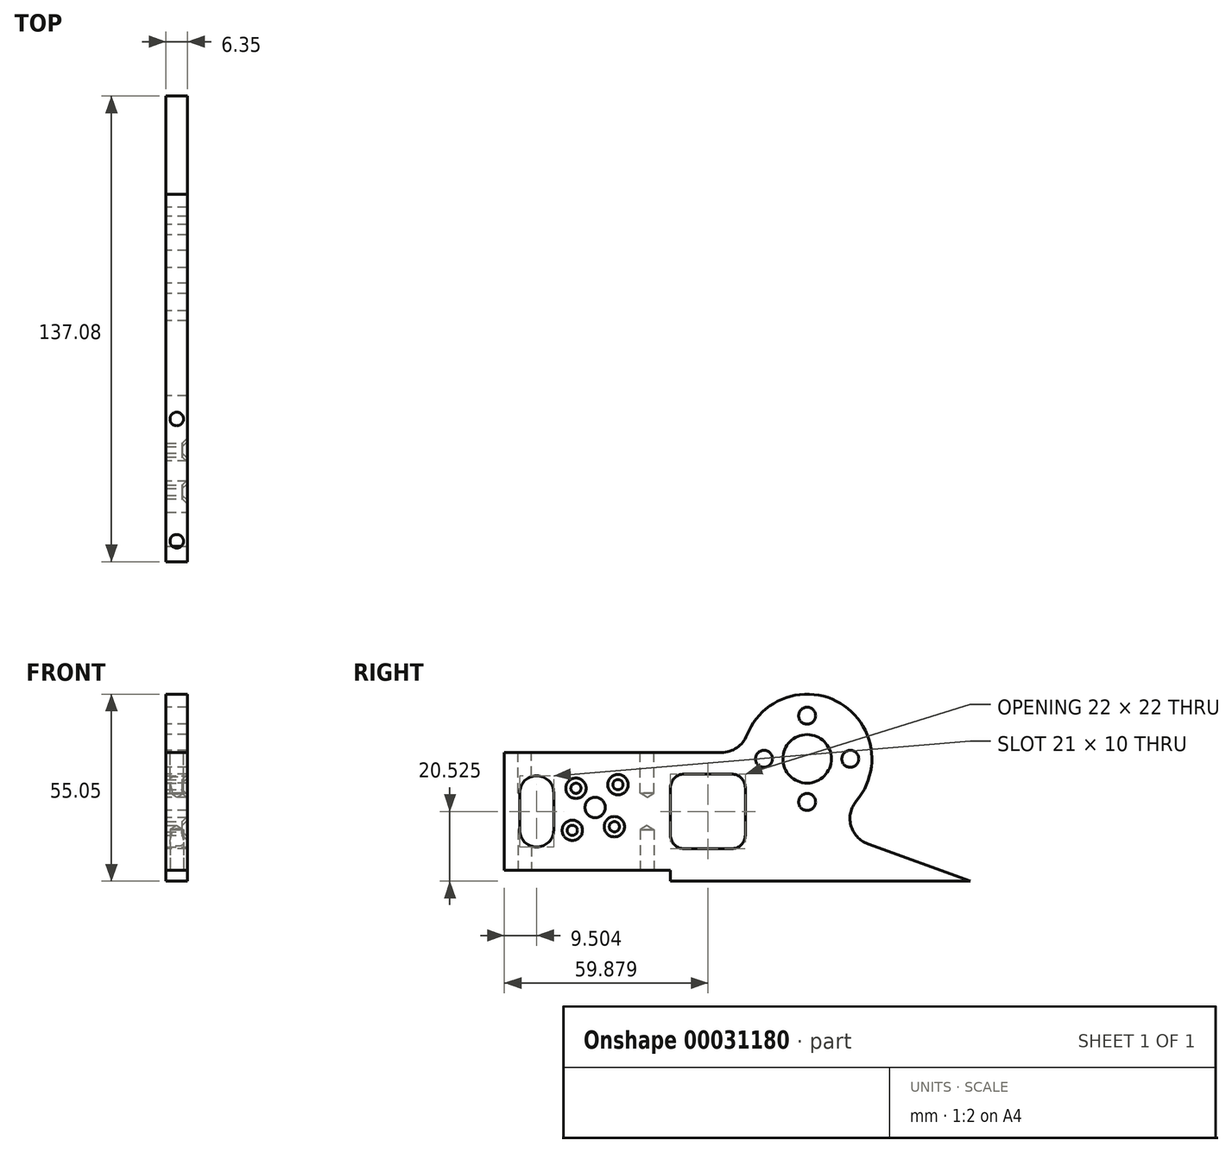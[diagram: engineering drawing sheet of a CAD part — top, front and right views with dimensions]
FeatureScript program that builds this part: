
annotation { "Feature Type Name" : "Feature", "Feature Type Description" : "" }
export const myFeature = defineFeature(function(context is Context, id is Id, definition is map)
    precondition{}
    {
        {
            var Q0;
            Q0=qCreatedBy(makeId("Right.planeOp"),FACE);
            var sketch = newSketch(context, id + "F0", { "sketchPlane" : qUnion([Q0])});
            skCircle(sketch, "E0", {"center": v(0, 0) * mm, "radius": 7.14 * mm});
            skArc(sketch, "E1", {"start": v(14.52, -12.34) * mm, "mid": v(9.78, 16.35) * mm, "end": v(-17.74, 6.95) * mm});
            skCircle(sketch, "E2", {"center": v(0, 0) * mm, "radius": 12.7 * mm, "construction": true});
            skCircle(sketch, "E3", {"center": v(0, 12.7) * mm, "radius": 2.5 * mm});
            skCircle(sketch, "E4", {"center": v(-12.7, 0) * mm, "radius": 2.5 * mm});
            skCircle(sketch, "E5", {"center": v(12.7, 0) * mm, "radius": 2.5 * mm});
            skCircle(sketch, "E6", {"center": v(0, -12.7) * mm, "radius": 2.5 * mm});
            skCircle(sketch, "E7", {"center": v(0, 0) * mm, "radius": 33.85 * mm, "construction": true});
            skLineSegment(sketch, "E8", {"start": v(48, -36) * mm, "end": v(17.88, -25.04) * mm});
            skArc(sketch, "E9.filletArc", {"start": v(14.52, -12.34) * mm, "mid": v(12.88, -19.56) * mm, "end": v(17.88, -25.04) * mm});
            skLineSegment(sketch, "E10.bottom", {"start": v(-127.08, -4.48) * mm, "end": v(-93.08, -4.48) * mm});
            skLineSegment(sketch, "E10.top", {"start": v(-127.08, -26.48) * mm, "end": v(-93.08, -26.48) * mm});
            skLineSegment(sketch, "E10.right", {"start": v(-89.08, -8.48) * mm, "end": v(-89.08, -22.48) * mm});
            skLineSegment(sketch, "E11", {"start": v(-127.08, 1.87) * mm, "end": v(-127.08, -4.48) * mm});
            skLineSegment(sketch, "E12", {"start": v(-127.08, -26.48) * mm, "end": v(-127.08, -32.83) * mm});
            skLineSegment(sketch, "E13", {"start": v(-127.08, 1.87) * mm, "end": v(-25.18, 1.87) * mm});
            skCircle(sketch, "E14", {"center": v(-62.38, -14.33) * mm, "radius": 14 * mm, "construction": true});
            skLineSegment(sketch, "E15", {"start": v(-62.38, -14.33) * mm, "end": v(-62.38, 1.87) * mm, "construction": true});
            skLineSegment(sketch, "E16", {"start": v(-62.38, -14.33) * mm, "end": v(-62.38, -32.83) * mm, "construction": true});
            skLineSegment(sketch, "E17", {"start": v(-62.38, -14.33) * mm, "end": v(0, 0) * mm, "construction": true});
            skLineSegment(sketch, "E18.bottom", {"start": v(-40.2, 1.87) * mm, "end": v(-46.55, 1.87) * mm, "construction": true});
            skLineSegment(sketch, "E18.top", {"start": v(-40.2, -32.83) * mm, "end": v(-46.55, -32.83) * mm, "construction": true});
            skLineSegment(sketch, "E18.left", {"start": v(-40.2, 1.87) * mm, "end": v(-40.2, -32.83) * mm, "construction": true});
            skLineSegment(sketch, "E18.right", {"start": v(-46.55, 1.87) * mm, "end": v(-46.55, -32.83) * mm, "construction": true});
            skPoint(sketch, "E19.visualSharp", {"position": v(-18.96, 1.87) * mm});
            skArc(sketch, "E19.filletArc", {"start": v(-25.18, 1.87) * mm, "mid": v(-20.68, 3.27) * mm, "end": v(-17.74, 6.95) * mm});
            skPoint(sketch, "E20.visualSharp", {"position": v(-89.08, -4.48) * mm});
            skArc(sketch, "E20.filletArc", {"start": v(-89.08, -8.48) * mm, "mid": v(-90.25, -5.65) * mm, "end": v(-93.08, -4.48) * mm});
            skPoint(sketch, "E21.visualSharp", {"position": v(-89.08, -26.48) * mm});
            skArc(sketch, "E21.filletArc", {"start": v(-93.08, -26.48) * mm, "mid": v(-90.25, -25.3) * mm, "end": v(-89.08, -22.48) * mm});
            skLineSegment(sketch, "E22", {"start": v(-36.2, -4.48) * mm, "end": v(-22.2, -4.48) * mm});
            skLineSegment(sketch, "E23", {"start": v(-18.2, -8.48) * mm, "end": v(-18.2, -22.48) * mm});
            skLineSegment(sketch, "E24", {"start": v(-22.2, -26.48) * mm, "end": v(-36.2, -26.48) * mm});
            skLineSegment(sketch, "E25", {"start": v(-40.2, -22.48) * mm, "end": v(-40.2, -8.48) * mm});
            skPoint(sketch, "E26.visualSharp", {"position": v(-40.2, -4.48) * mm});
            skArc(sketch, "E26.filletArc", {"start": v(-36.2, -4.48) * mm, "mid": v(-39.03, -5.65) * mm, "end": v(-40.2, -8.48) * mm});
            skPoint(sketch, "E27.visualSharp", {"position": v(-18.2, -4.48) * mm});
            skArc(sketch, "E27.filletArc", {"start": v(-18.2, -8.48) * mm, "mid": v(-19.37, -5.65) * mm, "end": v(-22.2, -4.48) * mm});
            skPoint(sketch, "E28.visualSharp", {"position": v(-18.2, -26.48) * mm});
            skArc(sketch, "E28.filletArc", {"start": v(-22.2, -26.47) * mm, "mid": v(-19.37, -25.3) * mm, "end": v(-18.2, -22.48) * mm});
            skPoint(sketch, "E29.visualSharp", {"position": v(-40.2, -26.48) * mm});
            skArc(sketch, "E29.filletArc", {"start": v(-40.2, -22.48) * mm, "mid": v(-39.03, -25.3) * mm, "end": v(-36.2, -26.48) * mm});
            skCircle(sketch, "E30", {"center": v(-62.38, -14.33) * mm, "radius": 3 * mm});
            skLineSegment(sketch, "E31", {"start": v(-40.2, -32.83) * mm, "end": v(-127.08, -32.83) * mm});
            skLineSegment(sketch, "E32", {"start": v(-40.2, -32.83) * mm, "end": v(-40.2, -36) * mm});
            skLineSegment(sketch, "E33", {"start": v(-40.2, -36) * mm, "end": v(48, -36) * mm});
            skSolve(sketch);
        }
        {
            var Q0;
            Q0 = qSketchRegion(id + "F0", true);
            extrude(context, id + "F1", {"entities" : qUnion([Q0]), "depth" : 6.35 * mm});
        }
        {
            var Q0;
            Q0=makeQuery(id+"F1.opExtrude","CAP_FACE",FACE,{"disambiguationData":[OSD([sQuery(id+"F0.wireOp",EDGE,"E0"),sQuery(id+"F0.wireOp",EDGE,"E1"),sQuery(id+"F0.wireOp",EDGE,"E3"),sQuery(id+"F0.wireOp",EDGE,"E4"),sQuery(id+"F0.wireOp",EDGE,"E5"),sQuery(id+"F0.wireOp",EDGE,"E6"),sQuery(id+"F0.wireOp",EDGE,"d800da94-32d5-4916-a3c5-9d9b6c6d528f"),sQuery(id+"F0.wireOp",EDGE,"E8"),sQuery(id+"F0.wireOp",EDGE,"E9.filletArc"),sQuery(id+"F0.wireOp",EDGE,"E10.bottom"),sQuery(id+"F0.wireOp",EDGE,"E10.top"),sQuery(id+"F0.wireOp",EDGE,"E10.right"),sQuery(id+"F0.wireOp",EDGE,"E11"),sQuery(id+"F0.wireOp",EDGE,"E12"),sQuery(id+"F0.wireOp",EDGE,"E13"),sQuery(id+"F0.wireOp",EDGE,"E19.filletArc"),sQuery(id+"F0.wireOp",EDGE,"E20.filletArc"),sQuery(id+"F0.wireOp",EDGE,"E21.filletArc"),sQuery(id+"F0.wireOp",EDGE,"E22"),sQuery(id+"F0.wireOp",EDGE,"E23"),sQuery(id+"F0.wireOp",EDGE,"E24"),sQuery(id+"F0.wireOp",EDGE,"E25"),sQuery(id+"F0.wireOp",EDGE,"E26.filletArc"),sQuery(id+"F0.wireOp",EDGE,"E27.filletArc"),sQuery(id+"F0.wireOp",EDGE,"E28.filletArc"),sQuery(id+"F0.wireOp",EDGE,"E29.filletArc"),sQuery(id+"F0.wireOp",EDGE,"E30")])],"isStart":false});
            var sketch = newSketch(context, id + "F2", { "sketchPlane" : qUnion([Q0])});
            skCircle(sketch, "E34", {"center": v(-62.38, -14.33) * mm, "radius": 8 * mm, "construction": true});
            skCircle(sketch, "E35", {"center": v(-62.38, -14.33) * mm, "radius": 9.5 * mm, "construction": true});
            skPoint(sketch, "E36", {"position": v(-55.66, -7.6) * mm});
            skPoint(sketch, "E37", {"position": v(-68.03, -8.67) * mm});
            skPoint(sketch, "E38", {"position": v(-69.1, -21.04) * mm});
            skPoint(sketch, "E39", {"position": v(-56.72, -19.98) * mm});
            skLineSegment(sketch, "E40", {"start": v(-68.03, -8.67) * mm, "end": v(-56.72, -19.98) * mm, "construction": true});
            skLineSegment(sketch, "E41", {"start": v(-55.66, -7.6) * mm, "end": v(-69.1, -21.04) * mm, "construction": true});
            skLineSegment(sketch, "E42", {"start": v(-62.38, -14.33) * mm, "end": v(-62.38, 1.87) * mm, "construction": true});
            skSolve(sketch);
        }
        {
            var Q0;
            Q0=sQuery(id+"F2.wireOp",VERTEX,"E36");
            var Q1;
            Q1=sQuery(id+"F2.wireOp",VERTEX,"E37");
            var Q2;
            Q2=sQuery(id+"F2.wireOp",VERTEX,"E38");
            var Q3;
            Q3=sQuery(id+"F2.wireOp",VERTEX,"E39");
            var Q4;
            Q4=makeQuery(id+"F1.opExtrude","SWEPT_BODY",BODY,{"disambiguationData":[OSD([sQuery(id+"F0.wireOp",EDGE,"E0"),sQuery(id+"F0.wireOp",EDGE,"E1"),sQuery(id+"F0.wireOp",EDGE,"E3"),sQuery(id+"F0.wireOp",EDGE,"E4"),sQuery(id+"F0.wireOp",EDGE,"E5"),sQuery(id+"F0.wireOp",EDGE,"E6"),sQuery(id+"F0.wireOp",EDGE,"d800da94-32d5-4916-a3c5-9d9b6c6d528f"),sQuery(id+"F0.wireOp",EDGE,"E8"),sQuery(id+"F0.wireOp",EDGE,"E9.filletArc"),sQuery(id+"F0.wireOp",EDGE,"E10.bottom"),sQuery(id+"F0.wireOp",EDGE,"E10.top"),sQuery(id+"F0.wireOp",EDGE,"E10.right"),sQuery(id+"F0.wireOp",EDGE,"E11"),sQuery(id+"F0.wireOp",EDGE,"E12"),sQuery(id+"F0.wireOp",EDGE,"E13"),sQuery(id+"F0.wireOp",EDGE,"E19.filletArc"),sQuery(id+"F0.wireOp",EDGE,"E20.filletArc"),sQuery(id+"F0.wireOp",EDGE,"E21.filletArc"),sQuery(id+"F0.wireOp",EDGE,"E22"),sQuery(id+"F0.wireOp",EDGE,"E23"),sQuery(id+"F0.wireOp",EDGE,"E24"),sQuery(id+"F0.wireOp",EDGE,"E25"),sQuery(id+"F0.wireOp",EDGE,"E26.filletArc"),sQuery(id+"F0.wireOp",EDGE,"E27.filletArc"),sQuery(id+"F0.wireOp",EDGE,"E28.filletArc"),sQuery(id+"F0.wireOp",EDGE,"E29.filletArc"),sQuery(id+"F0.wireOp",EDGE,"E30")])]});
            hole(context, id + "F3", {"style" : HoleStyle.C_SINK, "holeDiameter" : 3 * mm, "cSinkDiameter" : 6 * mm, "endStyle" : HoleEndStyle.THROUGH, "locations" : qUnion([Q0, Q1, Q2, Q3]), "scope" : qUnion([Q4]), "cSinkAngle" : 90 * degree});
        }
        {
            var Q0;
            Q0=makeQuery(id+"F1.opExtrude","CAP_FACE",FACE,{"disambiguationData":[OSD([sQuery(id+"F0.wireOp",EDGE,"E0"),sQuery(id+"F0.wireOp",EDGE,"E1"),sQuery(id+"F0.wireOp",EDGE,"E3"),sQuery(id+"F0.wireOp",EDGE,"E4"),sQuery(id+"F0.wireOp",EDGE,"E5"),sQuery(id+"F0.wireOp",EDGE,"E6"),sQuery(id+"F0.wireOp",EDGE,"d800da94-32d5-4916-a3c5-9d9b6c6d528f"),sQuery(id+"F0.wireOp",EDGE,"E8"),sQuery(id+"F0.wireOp",EDGE,"E9.filletArc"),sQuery(id+"F0.wireOp",EDGE,"E10.bottom"),sQuery(id+"F0.wireOp",EDGE,"E10.top"),sQuery(id+"F0.wireOp",EDGE,"E10.right"),sQuery(id+"F0.wireOp",EDGE,"E11"),sQuery(id+"F0.wireOp",EDGE,"E12"),sQuery(id+"F0.wireOp",EDGE,"E13"),sQuery(id+"F0.wireOp",EDGE,"E19.filletArc"),sQuery(id+"F0.wireOp",EDGE,"E20.filletArc"),sQuery(id+"F0.wireOp",EDGE,"E21.filletArc"),sQuery(id+"F0.wireOp",EDGE,"E22"),sQuery(id+"F0.wireOp",EDGE,"E23"),sQuery(id+"F0.wireOp",EDGE,"E24"),sQuery(id+"F0.wireOp",EDGE,"E25"),sQuery(id+"F0.wireOp",EDGE,"E26.filletArc"),sQuery(id+"F0.wireOp",EDGE,"E27.filletArc"),sQuery(id+"F0.wireOp",EDGE,"E28.filletArc"),sQuery(id+"F0.wireOp",EDGE,"E29.filletArc"),sQuery(id+"F0.wireOp",EDGE,"E30")])],"isStart":false});
            var sketch = newSketch(context, id + "F4", { "sketchPlane" : qUnion([Q0])});
            skLineSegment(sketch, "E43", {"start": v(-79.58, -9.98) * mm, "end": v(-79.58, -20.98) * mm});
            skArc(sketch, "E44.0.startCap", {"start": v(-84.58, -9.98) * mm, "mid": v(-79.58, -4.98) * mm, "end": v(-74.58, -9.98) * mm});
            skArc(sketch, "E44.0.endCap", {"start": v(-74.58, -20.98) * mm, "mid": v(-79.58, -25.98) * mm, "end": v(-84.58, -20.98) * mm});
            skLineSegment(sketch, "E44.0.left", {"start": v(-74.58, -9.98) * mm, "end": v(-74.58, -20.98) * mm});
            skLineSegment(sketch, "E44.0.right", {"start": v(-84.58, -9.98) * mm, "end": v(-84.58, -20.98) * mm});
            skLineSegment(sketch, "E45", {"start": v(-79.58, -9.98) * mm, "end": v(-79.58, 1.87) * mm, "construction": true});
            skLineSegment(sketch, "E46", {"start": v(-79.58, -20.98) * mm, "end": v(-79.58, -32.83) * mm, "construction": true});
            skPoint(sketch, "E46.endSnap0", {"position": v(-79.58, -25.98) * mm});
            skSolve(sketch);
        }
        {
            var Q0;
            Q0 = qSketchRegion(id + "F4", true);
            extrude(context, id + "F5", {"entities" : qUnion([Q0]), "operationType" : NewBodyOperationType.REMOVE, "oppositeDirection" : true, "depth" : 25 * mm});
        }
        {
            var Q0;
            Q0=makeQuery(id+"F1.opExtrude","SWEPT_FACE",FACE,{"disambiguationData":[OSD([sQuery(id+"F0.wireOp",EDGE,"E13")])]});
            var sketch = newSketch(context, id + "F6", { "sketchPlane" : qUnion([Q0])});
            skLineSegment(sketch, "E47.bottom", {"start": v(0, -127.08) * mm, "end": v(6.35, -127.08) * mm});
            skLineSegment(sketch, "E47.top", {"start": v(0, -89.08) * mm, "end": v(6.35, -89.08) * mm});
            skLineSegment(sketch, "E47.left", {"start": v(0, -127.08) * mm, "end": v(0, -89.08) * mm});
            skLineSegment(sketch, "E47.right", {"start": v(6.35, -127.08) * mm, "end": v(6.35, -89.08) * mm});
            skSolve(sketch);
        }
        {
            var Q0;
            Q0 = qSketchRegion(id + "F6", true);
            extrude(context, id + "F7", {"entities" : qUnion([Q0]), "operationType" : NewBodyOperationType.REMOVE, "endBound" : BoundingType.THROUGH_ALL, "oppositeDirection" : true, "depth" : 25 * mm});
        }
        {
            var Q0;
            Q0=makeQuery(id+"F1.opExtrude","SWEPT_FACE",FACE,{"disambiguationData":[OSD([sQuery(id+"F0.wireOp",EDGE,"E13")])]});
            var sketch = newSketch(context, id + "F8", { "sketchPlane" : qUnion([Q0])});
            skPoint(sketch, "E48", {"position": v(3.18, -83.08) * mm});
            skPoint(sketch, "E49", {"position": v(3.17, -47.08) * mm});
            skLineSegment(sketch, "E50", {"start": v(3.18, -89.08) * mm, "end": v(3.18, -83.08) * mm, "construction": true});
            skLineSegment(sketch, "E51", {"start": v(3.17, -47.08) * mm, "end": v(3.18, -83.08) * mm, "construction": true});
            skSolve(sketch);
        }
        {
            var Q0;
            Q0=sQuery(id+"F8.wireOp",VERTEX,"E49");
            var Q1;
            Q1=sQuery(id+"F8.wireOp",VERTEX,"E48");
            var Q2;
            Q2=makeQuery(id+"F1.opExtrude","SWEPT_BODY",BODY,{"disambiguationData":[OSD([sQuery(id+"F0.wireOp",EDGE,"E0"),sQuery(id+"F0.wireOp",EDGE,"E1"),sQuery(id+"F0.wireOp",EDGE,"E3"),sQuery(id+"F0.wireOp",EDGE,"E4"),sQuery(id+"F0.wireOp",EDGE,"E5"),sQuery(id+"F0.wireOp",EDGE,"E6"),sQuery(id+"F0.wireOp",EDGE,"E8"),sQuery(id+"F0.wireOp",EDGE,"E9.filletArc"),sQuery(id+"F0.wireOp",EDGE,"E10.bottom"),sQuery(id+"F0.wireOp",EDGE,"E10.top"),sQuery(id+"F0.wireOp",EDGE,"E10.right"),sQuery(id+"F0.wireOp",EDGE,"E11"),sQuery(id+"F0.wireOp",EDGE,"E12"),sQuery(id+"F0.wireOp",EDGE,"E13"),sQuery(id+"F0.wireOp",EDGE,"E19.filletArc"),sQuery(id+"F0.wireOp",EDGE,"E20.filletArc"),sQuery(id+"F0.wireOp",EDGE,"E21.filletArc"),sQuery(id+"F0.wireOp",EDGE,"E22"),sQuery(id+"F0.wireOp",EDGE,"E23"),sQuery(id+"F0.wireOp",EDGE,"E24"),sQuery(id+"F0.wireOp",EDGE,"E25"),sQuery(id+"F0.wireOp",EDGE,"E26.filletArc"),sQuery(id+"F0.wireOp",EDGE,"E27.filletArc"),sQuery(id+"F0.wireOp",EDGE,"E28.filletArc"),sQuery(id+"F0.wireOp",EDGE,"E29.filletArc"),sQuery(id+"F0.wireOp",EDGE,"E30"),sQuery(id+"F0.wireOp",EDGE,"E31"),sQuery(id+"F0.wireOp",EDGE,"E32"),sQuery(id+"F0.wireOp",EDGE,"E33")])]});
            hole(context, id + "F9", {"style" : HoleStyle.SIMPLE, "holeDiameter" : 4 * mm, "endStyle" : HoleEndStyle.BLIND, "holeDepth" : 12 * mm, "locations" : qUnion([Q0, Q1]), "scope" : qUnion([Q2])});
        }
        {
            var Q0;
            Q0=makeQuery(id+"F1.opExtrude","SWEPT_FACE",FACE,{"disambiguationData":[OSD([sQuery(id+"F0.wireOp",EDGE,"E31")])]});
            var sketch = newSketch(context, id + "F10", { "sketchPlane" : qUnion([Q0])});
            skPoint(sketch, "E52", {"position": v(3.18, 47.08) * mm});
            skPoint(sketch, "E53", {"position": v(3.18, 83.08) * mm});
            skLineSegment(sketch, "E54", {"start": v(3.17, 89.08) * mm, "end": v(3.18, 83.08) * mm, "construction": true});
            skLineSegment(sketch, "E55", {"start": v(3.18, 47.08) * mm, "end": v(3.18, 83.08) * mm, "construction": true});
            skSolve(sketch);
        }
        {
            var Q0;
            Q0=sQuery(id+"F10.wireOp",VERTEX,"E52");
            var Q1;
            Q1=sQuery(id+"F10.wireOp",VERTEX,"E53");
            var Q2;
            Q2=makeQuery(id+"F1.opExtrude","SWEPT_BODY",BODY,{"disambiguationData":[OSD([sQuery(id+"F0.wireOp",EDGE,"E0"),sQuery(id+"F0.wireOp",EDGE,"E1"),sQuery(id+"F0.wireOp",EDGE,"E3"),sQuery(id+"F0.wireOp",EDGE,"E4"),sQuery(id+"F0.wireOp",EDGE,"E5"),sQuery(id+"F0.wireOp",EDGE,"E6"),sQuery(id+"F0.wireOp",EDGE,"E8"),sQuery(id+"F0.wireOp",EDGE,"E9.filletArc"),sQuery(id+"F0.wireOp",EDGE,"E10.bottom"),sQuery(id+"F0.wireOp",EDGE,"E10.top"),sQuery(id+"F0.wireOp",EDGE,"E10.right"),sQuery(id+"F0.wireOp",EDGE,"E11"),sQuery(id+"F0.wireOp",EDGE,"E12"),sQuery(id+"F0.wireOp",EDGE,"E13"),sQuery(id+"F0.wireOp",EDGE,"E19.filletArc"),sQuery(id+"F0.wireOp",EDGE,"E20.filletArc"),sQuery(id+"F0.wireOp",EDGE,"E21.filletArc"),sQuery(id+"F0.wireOp",EDGE,"E22"),sQuery(id+"F0.wireOp",EDGE,"E23"),sQuery(id+"F0.wireOp",EDGE,"E24"),sQuery(id+"F0.wireOp",EDGE,"E25"),sQuery(id+"F0.wireOp",EDGE,"E26.filletArc"),sQuery(id+"F0.wireOp",EDGE,"E27.filletArc"),sQuery(id+"F0.wireOp",EDGE,"E28.filletArc"),sQuery(id+"F0.wireOp",EDGE,"E29.filletArc"),sQuery(id+"F0.wireOp",EDGE,"E30"),sQuery(id+"F0.wireOp",EDGE,"E31"),sQuery(id+"F0.wireOp",EDGE,"E32"),sQuery(id+"F0.wireOp",EDGE,"E33")])]});
            hole(context, id + "F11", {"style" : HoleStyle.SIMPLE, "holeDiameter" : 4 * mm, "endStyle" : HoleEndStyle.BLIND, "holeDepth" : 12 * mm, "locations" : qUnion([Q0, Q1]), "scope" : qUnion([Q2])});
        }
    });
